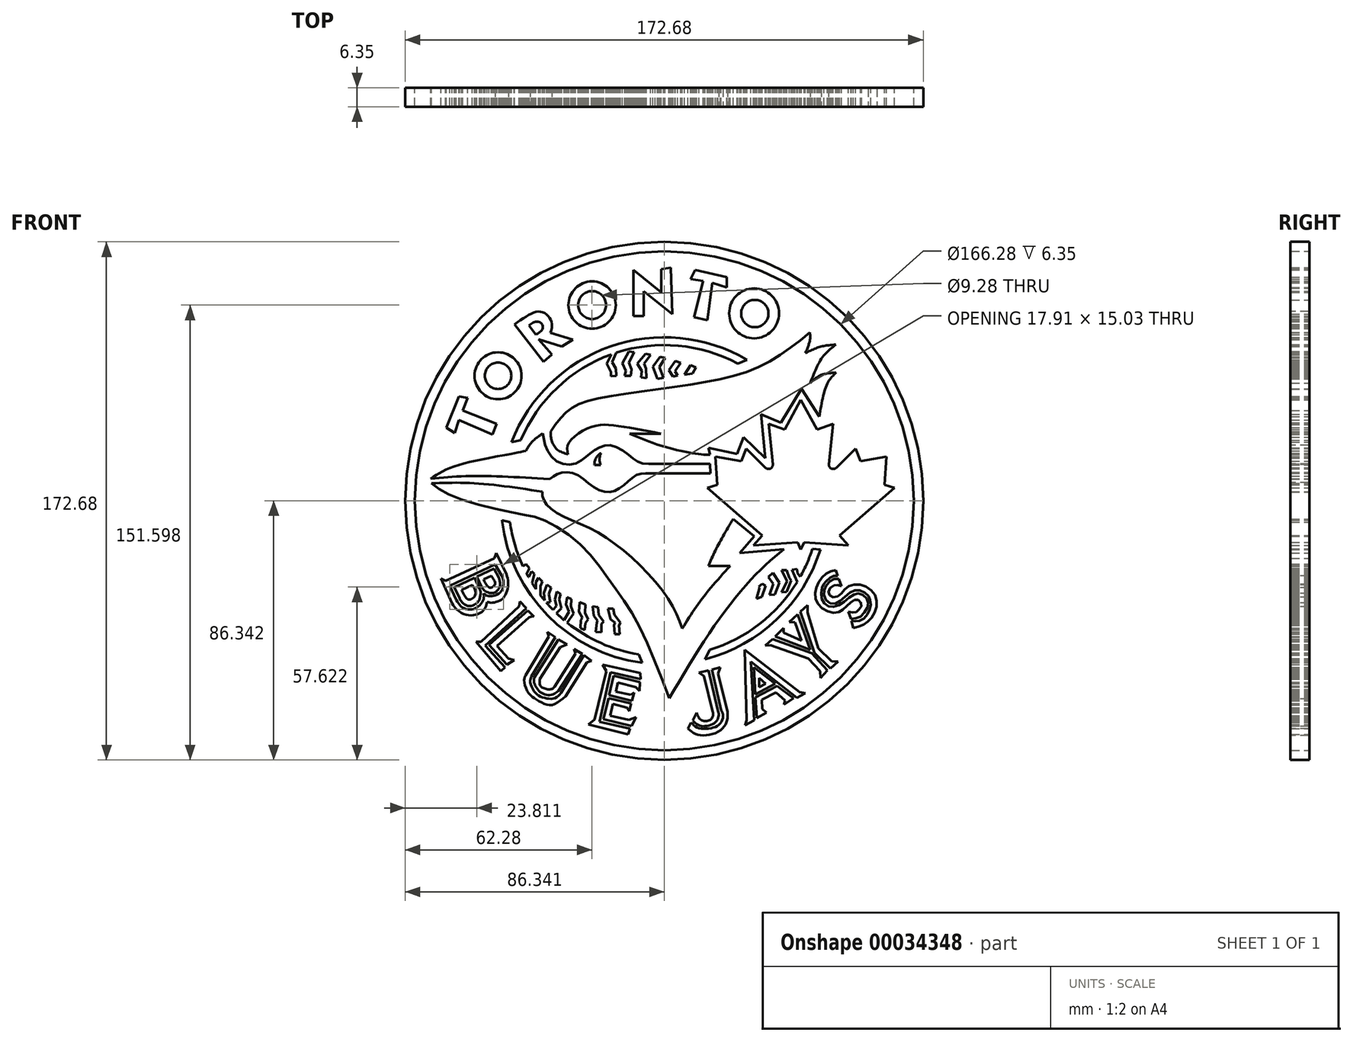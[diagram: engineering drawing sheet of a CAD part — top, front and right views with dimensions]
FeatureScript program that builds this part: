
annotation { "Feature Type Name" : "Feature", "Feature Type Description" : "" }
export const myFeature = defineFeature(function(context is Context, id is Id, definition is map)
    precondition{}
    {
        {
            var Q0;
            Q0=qCreatedBy(makeId("Front.planeOp"),FACE);
            var sketch = newSketch(context, id + "F0", { "sketchPlane" : qUnion([Q0])});
            skCircle(sketch, "E0", {"center": v(103.03, 95.92) * mm, "radius": 91.5 * mm});
            skCircle(sketch, "E1", {"center": v(103.03, 95.92) * mm, "radius": 88.78 * mm});
            skCircle(sketch, "E2", {"center": v(103.03, 95.92) * mm, "radius": 86.34 * mm});
            skCircle(sketch, "E3", {"center": v(103.03, 95.92) * mm, "radius": 83.14 * mm});
            skArc(sketch, "E4", {"start": v(48.91, 89.4) * mm, "mid": v(64.18, 57.7) * mm, "end": v(95.65, 41.92) * mm});
            skArc(sketch, "E5", {"start": v(51.6, 88.83) * mm, "mid": v(65.81, 59.73) * mm, "end": v(94.5, 44.71) * mm});
            skLineSegment(sketch, "E6", {"start": v(52.14, 115.45) * mm, "end": v(55.2, 116.12) * mm});
            skLineSegment(sketch, "E7", {"start": v(48.91, 89.4) * mm, "end": v(51.6, 88.83) * mm});
            skLineSegment(sketch, "E8", {"start": v(94.5, 44.71) * mm, "end": v(95.65, 41.92) * mm});
            skLineSegment(sketch, "E9", {"start": v(118.16, 46.26) * mm, "end": v(116.6, 43.13) * mm});
            skArc(sketch, "E10.trimOffspring", {"start": v(118.16, 46.26) * mm, "mid": v(139.41, 58.89) * mm, "end": v(152.42, 79.91) * mm});
            skArc(sketch, "E11.trimOffspring", {"start": v(116.6, 43.13) * mm, "mid": v(140.56, 56.4) * mm, "end": v(155.05, 79.63) * mm});
            skLineSegment(sketch, "E12", {"start": v(152.42, 79.91) * mm, "end": v(155.05, 79.63) * mm});
            skLineSegment(sketch, "E13", {"start": v(127.53, 141.7) * mm, "end": v(130.6, 142.95) * mm});
            skArc(sketch, "E14.trimOffspring", {"start": v(130.6, 142.95) * mm, "mid": v(85, 147.36) * mm, "end": v(52.14, 115.45) * mm});
            skArc(sketch, "E15.trimOffspring", {"start": v(127.53, 141.7) * mm, "mid": v(85.72, 144.87) * mm, "end": v(55.2, 116.12) * mm});
            skLineSegment(sketch, "E16", {"start": v(148.56, 129.54) * mm, "end": v(148.56, 79.7) * mm, "construction": true});
            skLineSegment(sketch, "E17", {"start": v(148.56, 129.54) * mm, "end": v(143.12, 119.66) * mm});
            skLineSegment(sketch, "E18", {"start": v(143.12, 119.66) * mm, "end": v(137.77, 121.56) * mm});
            skLineSegment(sketch, "E19", {"start": v(137.77, 121.56) * mm, "end": v(139.22, 108.15) * mm});
            skArc(sketch, "E20", {"start": v(139.22, 108.15) * mm, "mid": v(138.36, 106.66) * mm, "end": v(136.67, 107.03) * mm});
            skLineSegment(sketch, "E21", {"start": v(136.67, 107.03) * mm, "end": v(130.34, 113.34) * mm});
            skLineSegment(sketch, "E22", {"start": v(130.34, 113.34) * mm, "end": v(128.69, 109.14) * mm});
            skLineSegment(sketch, "E23", {"start": v(128.69, 109.14) * mm, "end": v(120, 110.7) * mm});
            skLineSegment(sketch, "E24", {"start": v(120, 110.7) * mm, "end": v(120.67, 101.3) * mm});
            skLineSegment(sketch, "E25", {"start": v(120.67, 101.3) * mm, "end": v(117.33, 100.22) * mm});
            skLineSegment(sketch, "E26", {"start": v(117.33, 100.22) * mm, "end": v(135.67, 84.42) * mm});
            skLineSegment(sketch, "E27", {"start": v(135.67, 84.42) * mm, "end": v(132.77, 81.06) * mm});
            skLineSegment(sketch, "E28", {"start": v(132.77, 81.06) * mm, "end": v(147.48, 82.1) * mm});
            skLineSegment(sketch, "E29", {"start": v(147.48, 82.1) * mm, "end": v(148.56, 79.7) * mm});
            skLineSegment(sketch, "E30.MirrorCS", {"start": v(176.45, 101.3) * mm, "end": v(179.78, 100.22) * mm});
            skLineSegment(sketch, "E31.MirrorCS", {"start": v(161.45, 84.42) * mm, "end": v(164.34, 81.06) * mm});
            skLineSegment(sketch, "E32.MirrorCS", {"start": v(166.78, 113.34) * mm, "end": v(168.43, 109.14) * mm});
            skArc(sketch, "E33.MirrorCS", {"start": v(157.9, 108.15) * mm, "mid": v(158.76, 106.66) * mm, "end": v(160.44, 107.03) * mm});
            skLineSegment(sketch, "E34.MirrorCS", {"start": v(149.64, 82.1) * mm, "end": v(148.56, 79.7) * mm});
            skLineSegment(sketch, "E35.MirrorCS", {"start": v(164.34, 81.06) * mm, "end": v(149.64, 82.1) * mm});
            skLineSegment(sketch, "E36.MirrorCS", {"start": v(159.34, 121.56) * mm, "end": v(157.9, 108.15) * mm});
            skLineSegment(sketch, "E37.MirrorCS", {"start": v(154, 119.66) * mm, "end": v(159.34, 121.56) * mm});
            skLineSegment(sketch, "E38.MirrorCS", {"start": v(160.44, 107.03) * mm, "end": v(166.78, 113.34) * mm});
            skLineSegment(sketch, "E39.MirrorCS", {"start": v(177.1, 110.7) * mm, "end": v(176.45, 101.3) * mm});
            skLineSegment(sketch, "E40.MirrorCS", {"start": v(168.43, 109.14) * mm, "end": v(177.1, 110.7) * mm});
            skLineSegment(sketch, "E41.MirrorCS", {"start": v(148.56, 129.54) * mm, "end": v(154, 119.66) * mm});
            skLineSegment(sketch, "E42.MirrorCS", {"start": v(179.78, 100.22) * mm, "end": v(161.45, 84.42) * mm});
            skFitSpline(sketch, "E43", {"points": [v(65.16, 119.04) * mm, v(70.66, 125.76) * mm, v(79.5, 129.73) * mm, v(109.43, 134.3) * mm, v(134.92, 140.72) * mm, v(151.56, 152.02) * mm], "startDerivative": vector(37.03, 53.23) * mm, "endDerivative": vector(73.6, 59.4) * mm});
            skFitSpline(sketch, "E44", {"points": [v(70.96, 111.41) * mm, v(71.11, 115.08) * mm, v(78.29, 120.42) * mm, v(86.53, 121.03) * mm, v(101.9, 118.34) * mm], "startDerivative": vector(-4.68, 21.83) * mm, "endDerivative": vector(49.53, -9.74) * mm});
            skFitSpline(sketch, "E45", {"points": [v(91.5, 118.29) * mm, v(103.51, 113.83) * mm, v(114.3, 111.55) * mm, v(118.26, 111.24) * mm], "startDerivative": vector(29.11, -12.06) * mm, "endDerivative": vector(15.42, -0.64) * mm});
            skFitSpline(sketch, "E46", {"points": [v(25.2, 103.34) * mm, v(32.9, 107.34) * mm, v(50.65, 111.34) * mm, v(56.95, 112.56) * mm], "startDerivative": vector(20.92, 13.84) * mm, "endDerivative": vector(19.98, 4) * mm});
            skFitSpline(sketch, "E47", {"points": [v(25.44, 101.77) * mm, v(33.14, 97.16) * mm, v(53.44, 91.83) * mm, v(62.71, 89.59) * mm, v(75.1, 81.35) * mm, v(85.16, 68.85) * mm, v(93.88, 55.68) * mm, v(104.66, 30.12) * mm], "startDerivative": vector(57.19, -43.62) * mm, "endDerivative": vector(55.75, -147.62) * mm});
            skFitSpline(sketch, "E48", {"points": [v(142.86, 79.86) * mm, v(133.46, 71.3) * mm, v(119.83, 54.38) * mm, v(104.66, 30.12) * mm], "startDerivative": vector(-34.83, -29.36) * mm, "endDerivative": vector(-37.83, -63.75) * mm});
            skFitSpline(sketch, "E49", {"points": [v(62.36, 98.98) * mm, v(62.87, 96.15) * mm, v(67, 92.01) * mm, v(78.22, 86.76) * mm, v(92.16, 77.06) * mm, v(104.58, 62.92) * mm, v(109.02, 53.43) * mm], "startDerivative": vector(1.07, -31.73) * mm, "endDerivative": vector(20.44, -54.43) * mm});
            skFitSpline(sketch, "E50", {"points": [v(109.02, 53.43) * mm, v(115.59, 63.23) * mm, v(124.98, 74.23) * mm], "startDerivative": vector(12.88, 20.58) * mm, "endDerivative": vector(18.93, 21.03) * mm});
            skFitSpline(sketch, "E51", {"points": [v(126, 89.89) * mm, v(120.94, 81.1) * mm, v(117.7, 74.23) * mm], "startDerivative": vector(-10.08, -16.82) * mm, "endDerivative": vector(-6.4, -14.44) * mm});
            skFitSpline(sketch, "E52", {"points": [v(62.56, 118.37) * mm, v(63.68, 113.62) * mm, v(67.72, 108.78) * mm, v(73.67, 108.47) * mm, v(77.51, 111.1) * mm, v(81.25, 113.62) * mm, v(85.29, 114.43) * mm, v(91.15, 111.2) * mm, v(94.78, 108.68) * mm, v(100.03, 108.27) * mm], "startDerivative": vector(6.02, -43.1) * mm, "endDerivative": vector(50.83, 1.53) * mm});
            skFitSpline(sketch, "E53", {"points": [v(64.79, 103.12) * mm, v(68.3, 105.12) * mm, v(73.58, 104.78) * mm, v(79.92, 100.18) * mm, v(85.37, 98.95) * mm, v(89.97, 101.53) * mm, v(94.06, 104.67) * mm, v(98.1, 105.06) * mm, v(100.85, 105.06) * mm], "startDerivative": vector(28.53, 20.8) * mm, "endDerivative": vector(27.63, 0.43) * mm});
            skFitSpline(sketch, "E54", {"points": [v(62.56, 118.37) * mm, v(61.23, 117.5) * mm, v(58.68, 115.27) * mm, v(56.95, 112.56) * mm], "startDerivative": vector(-4.68, -2.94) * mm, "endDerivative": vector(-4.02, -7.62) * mm});
            skFitSpline(sketch, "E55", {"points": [v(65.16, 119.04) * mm, v(65.44, 116.26) * mm, v(67.25, 113.1) * mm, v(70.96, 111.41) * mm], "startDerivative": vector(0.16, -9.06) * mm, "endDerivative": vector(11.34, -3.4) * mm});
            skFitSpline(sketch, "E56", {"points": [v(91.5, 118.29) * mm, v(101.9, 118.34) * mm], "startDerivative": vector(10.39, 0.05) * mm, "endDerivative": vector(10.39, 0.05) * mm});
            skLineSegment(sketch, "E57", {"start": v(118.26, 111.24) * mm, "end": v(117.8, 113.52) * mm});
            skLineSegment(sketch, "E58", {"start": v(117.8, 113.52) * mm, "end": v(127.26, 111.55) * mm});
            skLineSegment(sketch, "E59", {"start": v(127.26, 111.55) * mm, "end": v(129.43, 117.08) * mm});
            skLineSegment(sketch, "E60", {"start": v(129.43, 117.08) * mm, "end": v(136.65, 110.13) * mm});
            skLineSegment(sketch, "E61", {"start": v(136.65, 110.13) * mm, "end": v(135.36, 124.82) * mm});
            skLineSegment(sketch, "E62", {"start": v(135.36, 124.82) * mm, "end": v(141.96, 122.02) * mm});
            skLineSegment(sketch, "E63", {"start": v(141.96, 122.02) * mm, "end": v(148.7, 133.3) * mm});
            skLineSegment(sketch, "E64", {"start": v(148.7, 133.3) * mm, "end": v(154.7, 124.04) * mm});
            skFitSpline(sketch, "E65", {"points": [v(151.56, 152.02) * mm, v(151.56, 149.4) * mm, v(150.04, 145.15) * mm], "startDerivative": vector(0.58, -5.75) * mm, "endDerivative": vector(-3.44, -7.9) * mm});
            skFitSpline(sketch, "E66", {"points": [v(150.04, 145.15) * mm, v(155.23, 147.32) * mm, v(160.17, 147.96) * mm], "startDerivative": vector(10.04, 4.97) * mm, "endDerivative": vector(10.22, 0.62) * mm});
            skFitSpline(sketch, "E67", {"points": [v(160.17, 147.96) * mm, v(155.62, 143.57) * mm, v(151.67, 135.16) * mm], "startDerivative": vector(-10.7, -8.46) * mm, "endDerivative": vector(-6.44, -16.87) * mm});
            skFitSpline(sketch, "E68", {"points": [v(151.67, 135.16) * mm, v(155.13, 137.78) * mm, v(160.32, 138.67) * mm], "startDerivative": vector(6.64, 6.4) * mm, "endDerivative": vector(10.59, 0.7) * mm});
            skFitSpline(sketch, "E69", {"points": [v(160.32, 138.67) * mm, v(157.35, 134.97) * mm, v(154.7, 124.04) * mm], "startDerivative": vector(-8.15, -7.72) * mm, "endDerivative": vector(-3.43, -20.64) * mm});
            skLineSegment(sketch, "E70", {"start": v(100.03, 108.27) * mm, "end": v(118.29, 108.27) * mm});
            skLineSegment(sketch, "E71", {"start": v(118.29, 108.27) * mm, "end": v(118.43, 105.08) * mm});
            skLineSegment(sketch, "E72", {"start": v(118.43, 105.08) * mm, "end": v(100.85, 105.06) * mm});
            skFitSpline(sketch, "E73", {"points": [v(25.2, 103.34) * mm, v(40.41, 104.2) * mm, v(64.79, 103.12) * mm], "startDerivative": vector(32.45, 2.81) * mm, "endDerivative": vector(46.2, -3.04) * mm});
            skFitSpline(sketch, "E74", {"points": [v(25.44, 101.77) * mm, v(40.11, 101.77) * mm, v(62.36, 98.98) * mm], "startDerivative": vector(31.15, 1.13) * mm, "endDerivative": vector(42.3, -6.44) * mm});
            skLineSegment(sketch, "E75", {"start": v(126, 89.89) * mm, "end": v(132.96, 84.08) * mm});
            skLineSegment(sketch, "E76", {"start": v(132.96, 84.08) * mm, "end": v(128.14, 78.59) * mm});
            skLineSegment(sketch, "E77", {"start": v(128.14, 78.59) * mm, "end": v(142.86, 79.86) * mm});
            skLineSegment(sketch, "E78", {"start": v(124.98, 74.23) * mm, "end": v(117.7, 74.23) * mm});
            skCircle(sketch, "E79", {"center": v(133.2, 158.35) * mm, "radius": 4.55 * mm});
            skCircle(sketch, "E80", {"center": v(132.99, 158.42) * mm, "radius": 8.32 * mm});
            skLineSegment(sketch, "E81", {"start": v(117.34, 156.16) * mm, "end": v(112.99, 157.08) * mm});
            skLineSegment(sketch, "E82", {"start": v(112.99, 157.08) * mm, "end": v(115.93, 169.2) * mm});
            skLineSegment(sketch, "E83", {"start": v(115.93, 169.2) * mm, "end": v(111.8, 169.9) * mm});
            skLineSegment(sketch, "E84", {"start": v(111.8, 169.9) * mm, "end": v(113.28, 172.88) * mm});
            skLineSegment(sketch, "E85", {"start": v(113.28, 172.88) * mm, "end": v(123.86, 170.47) * mm});
            skLineSegment(sketch, "E86", {"start": v(123.86, 170.47) * mm, "end": v(123.86, 167) * mm});
            skLineSegment(sketch, "E87", {"start": v(123.86, 167) * mm, "end": v(118.98, 168.56) * mm});
            skLineSegment(sketch, "E88", {"start": v(118.98, 168.56) * mm, "end": v(117.34, 156.16) * mm});
            skLineSegment(sketch, "E89", {"start": v(105.18, 173.64) * mm, "end": v(105.75, 158.2) * mm});
            skLineSegment(sketch, "E90", {"start": v(105.75, 158.2) * mm, "end": v(96.18, 165.76) * mm});
            skLineSegment(sketch, "E91", {"start": v(96.18, 165.76) * mm, "end": v(96.18, 157.5) * mm});
            skLineSegment(sketch, "E92", {"start": v(96.18, 157.5) * mm, "end": v(92.75, 157.5) * mm});
            skLineSegment(sketch, "E93", {"start": v(92.75, 157.5) * mm, "end": v(92.75, 172.85) * mm});
            skLineSegment(sketch, "E94", {"start": v(92.75, 172.85) * mm, "end": v(101.96, 165.43) * mm});
            skLineSegment(sketch, "E95", {"start": v(101.96, 165.43) * mm, "end": v(101.96, 173.11) * mm});
            skLineSegment(sketch, "E96", {"start": v(101.96, 173.11) * mm, "end": v(105.18, 173.64) * mm});
            skCircle(sketch, "E97", {"center": v(78.97, 161.18) * mm, "radius": 4.64 * mm});
            skCircle(sketch, "E98", {"center": v(78.97, 161.18) * mm, "radius": 7.88 * mm});
            skCircle(sketch, "E99", {"center": v(47.64, 137.6) * mm, "radius": 7.83 * mm});
            skCircle(sketch, "E100", {"center": v(47.64, 137.6) * mm, "radius": 4.42 * mm});
            skLineSegment(sketch, "E101", {"start": v(47.13, 121.57) * mm, "end": v(35.88, 126.05) * mm});
            skLineSegment(sketch, "E102", {"start": v(35.88, 126.05) * mm, "end": v(37.5, 130.2) * mm});
            skLineSegment(sketch, "E103", {"start": v(37.5, 130.2) * mm, "end": v(34.61, 130.7) * mm});
            skLineSegment(sketch, "E104", {"start": v(34.61, 130.7) * mm, "end": v(30.33, 120.34) * mm});
            skLineSegment(sketch, "E105", {"start": v(30.33, 120.34) * mm, "end": v(33.17, 118.56) * mm});
            skLineSegment(sketch, "E106", {"start": v(33.17, 118.56) * mm, "end": v(34.54, 122.86) * mm});
            skLineSegment(sketch, "E107", {"start": v(34.54, 122.86) * mm, "end": v(45.75, 118.08) * mm});
            skLineSegment(sketch, "E108", {"start": v(45.75, 118.08) * mm, "end": v(47.13, 121.57) * mm});
            skLineSegment(sketch, "E109", {"start": v(53.13, 154.75) * mm, "end": v(62.81, 142.26) * mm});
            skLineSegment(sketch, "E110", {"start": v(62.81, 142.26) * mm, "end": v(65.59, 144.65) * mm});
            skLineSegment(sketch, "E111", {"start": v(65.59, 144.65) * mm, "end": v(61.17, 149.8) * mm});
            skLineSegment(sketch, "E112", {"start": v(61.17, 149.8) * mm, "end": v(68.92, 147.33) * mm});
            skLineSegment(sketch, "E113", {"start": v(68.92, 147.33) * mm, "end": v(72.5, 149.7) * mm});
            skLineSegment(sketch, "E114", {"start": v(72.5, 149.7) * mm, "end": v(65.1, 152) * mm});
            skFitSpline(sketch, "E115", {"points": [v(53.13, 154.75) * mm, v(59.13, 158.49) * mm, v(62.38, 158.83) * mm, v(65.01, 156.6) * mm, v(65.61, 153.93) * mm, v(65.1, 152) * mm], "startDerivative": vector(22.47, 15.8) * mm, "endDerivative": vector(-4.46, -12.2) * mm});
            skFitSpline(sketch, "E116", {"points": [v(57.9, 154.3) * mm, v(59.68, 155.53) * mm, v(61.75, 155.36) * mm, v(62.57, 153.73) * mm, v(61.64, 152.27) * mm, v(60.24, 151.35) * mm], "startDerivative": vector(7.67, 6.93) * mm, "endDerivative": vector(-7.62, -4.34) * mm});
            skLineSegment(sketch, "E117", {"start": v(57.9, 154.3) * mm, "end": v(60.24, 151.35) * mm});
            skLineSegment(sketch, "E118", {"start": v(40.25, 48.97) * mm, "end": v(48.5, 39.18) * mm});
            skLineSegment(sketch, "E119", {"start": v(48.5, 39.18) * mm, "end": v(49.91, 40.37) * mm});
            skLineSegment(sketch, "E120", {"start": v(49.91, 40.37) * mm, "end": v(43.3, 47.7) * mm});
            skLineSegment(sketch, "E121", {"start": v(43.3, 47.7) * mm, "end": v(57.13, 60.17) * mm});
            skLineSegment(sketch, "E122", {"start": v(57.13, 60.17) * mm, "end": v(54.87, 62.4) * mm});
            skLineSegment(sketch, "E123", {"start": v(59.58, 57.34) * mm, "end": v(57.5, 59.39) * mm});
            skLineSegment(sketch, "E124", {"start": v(57.5, 59.39) * mm, "end": v(44.68, 47.88) * mm});
            skLineSegment(sketch, "E125", {"start": v(44.68, 47.88) * mm, "end": v(50.6, 41.28) * mm});
            skLineSegment(sketch, "E126", {"start": v(50.6, 41.28) * mm, "end": v(52.98, 42.9) * mm});
            skLineSegment(sketch, "E127", {"start": v(52.98, 42.9) * mm, "end": v(51.13, 43.4) * mm});
            skLineSegment(sketch, "E128", {"start": v(51.13, 43.4) * mm, "end": v(47.24, 47.57) * mm});
            skLineSegment(sketch, "E129", {"start": v(47.24, 47.57) * mm, "end": v(57.89, 57.12) * mm});
            skLineSegment(sketch, "E130", {"start": v(57.89, 57.12) * mm, "end": v(59.14, 57.4) * mm});
            skLineSegment(sketch, "E131", {"start": v(59.14, 57.4) * mm, "end": v(59.58, 57.34) * mm});
            skLineSegment(sketch, "E132", {"start": v(95, 38.48) * mm, "end": v(82.45, 41.28) * mm});
            skLineSegment(sketch, "E133", {"start": v(82.45, 41.28) * mm, "end": v(83.69, 39.12) * mm});
            skLineSegment(sketch, "E134", {"start": v(83.69, 39.12) * mm, "end": v(79.75, 23.01) * mm});
            skLineSegment(sketch, "E135", {"start": v(79.75, 23.01) * mm, "end": v(77.74, 21.38) * mm});
            skLineSegment(sketch, "E136", {"start": v(77.74, 21.38) * mm, "end": v(91.03, 18.03) * mm});
            skLineSegment(sketch, "E137", {"start": v(91.03, 18.03) * mm, "end": v(91.65, 20.03) * mm});
            skLineSegment(sketch, "E138", {"start": v(91.65, 20.03) * mm, "end": v(81.45, 22.33) * mm});
            skLineSegment(sketch, "E139", {"start": v(81.45, 22.33) * mm, "end": v(85.14, 38.75) * mm});
            skLineSegment(sketch, "E140", {"start": v(85.14, 38.75) * mm, "end": v(95.15, 36.45) * mm});
            skLineSegment(sketch, "E141", {"start": v(95.15, 36.45) * mm, "end": v(95, 38.48) * mm});
            skLineSegment(sketch, "E142", {"start": v(94.95, 35.48) * mm, "end": v(86.1, 37.6) * mm});
            skLineSegment(sketch, "E143", {"start": v(86.1, 37.6) * mm, "end": v(84.57, 31.17) * mm});
            skLineSegment(sketch, "E144", {"start": v(84.57, 31.17) * mm, "end": v(92.28, 29.28) * mm});
            skLineSegment(sketch, "E145", {"start": v(92.28, 29.28) * mm, "end": v(92.97, 32.08) * mm});
            skLineSegment(sketch, "E146", {"start": v(92.97, 32.08) * mm, "end": v(91.8, 31.26) * mm});
            skLineSegment(sketch, "E147", {"start": v(91.8, 31.26) * mm, "end": v(86.87, 32.25) * mm});
            skLineSegment(sketch, "E148", {"start": v(86.87, 32.25) * mm, "end": v(87.55, 35.33) * mm});
            skLineSegment(sketch, "E149", {"start": v(87.55, 35.33) * mm, "end": v(93.45, 33.78) * mm});
            skLineSegment(sketch, "E150", {"start": v(93.45, 33.78) * mm, "end": v(94.77, 32.5) * mm});
            skLineSegment(sketch, "E151", {"start": v(94.77, 32.5) * mm, "end": v(94.95, 35.48) * mm});
            skLineSegment(sketch, "E152", {"start": v(84.5, 30.19) * mm, "end": v(92, 28.35) * mm});
            skLineSegment(sketch, "E153", {"start": v(92, 28.35) * mm, "end": v(91.41, 25.89) * mm});
            skLineSegment(sketch, "E154", {"start": v(91.41, 25.89) * mm, "end": v(90.56, 27) * mm});
            skLineSegment(sketch, "E155", {"start": v(90.56, 27) * mm, "end": v(85.9, 28.29) * mm});
            skLineSegment(sketch, "E156", {"start": v(85.9, 28.29) * mm, "end": v(85.02, 24.3) * mm});
            skLineSegment(sketch, "E157", {"start": v(85.02, 24.3) * mm, "end": v(91.25, 22.9) * mm});
            skLineSegment(sketch, "E158", {"start": v(91.25, 22.9) * mm, "end": v(93.6, 23.76) * mm});
            skLineSegment(sketch, "E159", {"start": v(93.6, 23.76) * mm, "end": v(92.11, 20.9) * mm});
            skLineSegment(sketch, "E160", {"start": v(92.11, 20.9) * mm, "end": v(82.77, 23.11) * mm});
            skLineSegment(sketch, "E161", {"start": v(82.77, 23.11) * mm, "end": v(84.5, 30.19) * mm});
            skLineSegment(sketch, "E162", {"start": v(28.6, 70) * mm, "end": v(30.08, 69.23) * mm});
            skLineSegment(sketch, "E163", {"start": v(30.08, 69.23) * mm, "end": v(46.46, 76.7) * mm});
            skLineSegment(sketch, "E164", {"start": v(46.46, 76.7) * mm, "end": v(47.04, 78.52) * mm});
            skLineSegment(sketch, "E165", {"start": v(47.04, 78.52) * mm, "end": v(50.44, 71.43) * mm});
            skLineSegment(sketch, "E166", {"start": v(28.6, 70) * mm, "end": v(32.27, 61.75) * mm});
            skLineSegment(sketch, "E167", {"start": v(40.25, 48.97) * mm, "end": v(42, 48.97) * mm});
            skLineSegment(sketch, "E168", {"start": v(42, 48.97) * mm, "end": v(54.6, 60.71) * mm});
            skLineSegment(sketch, "E169", {"start": v(54.6, 60.71) * mm, "end": v(54.87, 62.4) * mm});
            skLineSegment(sketch, "E170", {"start": v(64.02, 52.3) * mm, "end": v(66.72, 50.48) * mm});
            skLineSegment(sketch, "E171", {"start": v(66.72, 50.48) * mm, "end": v(58.73, 37.32) * mm});
            skLineSegment(sketch, "E172", {"start": v(70.66, 48) * mm, "end": v(67.73, 49.76) * mm});
            skLineSegment(sketch, "E173", {"start": v(67.73, 49.76) * mm, "end": v(59.6, 36.83) * mm});
            skLineSegment(sketch, "E174", {"start": v(72.95, 46.55) * mm, "end": v(73.47, 45.05) * mm});
            skLineSegment(sketch, "E175", {"start": v(73.47, 45.05) * mm, "end": v(66.45, 34) * mm});
            skLineSegment(sketch, "E176", {"start": v(72.95, 46.55) * mm, "end": v(75.7, 44.84) * mm});
            skLineSegment(sketch, "E177", {"start": v(75.7, 44.84) * mm, "end": v(67.7, 32.5) * mm});
            skLineSegment(sketch, "E178", {"start": v(61.56, 36.52) * mm, "end": v(68.36, 47.17) * mm});
            skLineSegment(sketch, "E179", {"start": v(68.36, 47.17) * mm, "end": v(70.66, 48) * mm});
            skLineSegment(sketch, "E180", {"start": v(70.15, 30.8) * mm, "end": v(77.21, 42.1) * mm});
            skLineSegment(sketch, "E181", {"start": v(77.21, 42.1) * mm, "end": v(78.77, 42.64) * mm});
            skLineSegment(sketch, "E182", {"start": v(78.77, 42.64) * mm, "end": v(76.2, 44.43) * mm});
            skLineSegment(sketch, "E183", {"start": v(76.2, 44.43) * mm, "end": v(68.68, 31.88) * mm});
            skFitSpline(sketch, "E184", {"points": [v(58.73, 37.32) * mm, v(58.36, 35.74) * mm, v(59.93, 32.06) * mm, v(62.76, 30.36) * mm, v(66.28, 30.06) * mm, v(68.68, 31.88) * mm], "startDerivative": vector(-4.2, -9.31) * mm, "endDerivative": vector(10.8, 11.52) * mm});
            skFitSpline(sketch, "E185", {"points": [v(59.6, 36.83) * mm, v(59.6, 35.55) * mm, v(60.61, 33.4) * mm, v(62.63, 31.6) * mm, v(65.56, 31.31) * mm, v(67.7, 32.5) * mm], "startDerivative": vector(-0.96, -8.08) * mm, "endDerivative": vector(9.5, 7.15) * mm});
            skFitSpline(sketch, "E186", {"points": [v(66.45, 34) * mm, v(65.38, 33.15) * mm, v(62.01, 34) * mm, v(61.56, 36.52) * mm], "startDerivative": vector(-2.97, -4.2) * mm, "endDerivative": vector(0.77, 8.19) * mm});
            skLineSegment(sketch, "E187", {"start": v(64.02, 52.3) * mm, "end": v(64.62, 50.68) * mm});
            skLineSegment(sketch, "E188", {"start": v(64.62, 50.68) * mm, "end": v(56.82, 37.76) * mm});
            skFitSpline(sketch, "E189", {"points": [v(56.82, 37.76) * mm, v(56.3, 36.04) * mm, v(57.8, 31.85) * mm, v(60.95, 29.38) * mm, v(65.2, 27.82) * mm, v(70.15, 30.8) * mm], "startDerivative": vector(-5.74, -10.9) * mm, "endDerivative": vector(20.48, 17.81) * mm});
            skLineSegment(sketch, "E190", {"start": v(31.55, 67.65) * mm, "end": v(46.66, 74.72) * mm});
            skLineSegment(sketch, "E191", {"start": v(46.66, 74.72) * mm, "end": v(48.82, 70.99) * mm});
            skLineSegment(sketch, "E192", {"start": v(31.55, 67.65) * mm, "end": v(33.76, 62.92) * mm});
            skLineSegment(sketch, "E193", {"start": v(34.8, 63.38) * mm, "end": v(33.01, 67.08) * mm});
            skLineSegment(sketch, "E194", {"start": v(33.01, 67.08) * mm, "end": v(39.75, 70.32) * mm});
            skLineSegment(sketch, "E195", {"start": v(39.75, 70.32) * mm, "end": v(41.43, 66.63) * mm});
            skLineSegment(sketch, "E196", {"start": v(42.2, 67.1) * mm, "end": v(40.53, 70.66) * mm});
            skLineSegment(sketch, "E197", {"start": v(40.53, 70.66) * mm, "end": v(46.28, 73.37) * mm});
            skLineSegment(sketch, "E198", {"start": v(46.28, 73.37) * mm, "end": v(47.9, 70.3) * mm});
            skLineSegment(sketch, "E199", {"start": v(42.8, 69.72) * mm, "end": v(45.33, 70.95) * mm});
            skLineSegment(sketch, "E200", {"start": v(35.46, 66.18) * mm, "end": v(39.02, 67.91) * mm});
            skFitSpline(sketch, "E201", {"points": [v(39.02, 67.91) * mm, v(39.91, 66.3) * mm, v(40.15, 64.94) * mm, v(39.22, 63.42) * mm, v(37.63, 63.07) * mm, v(36.58, 64.07) * mm, v(35.46, 66.18) * mm], "startDerivative": vector(5.81, -9.56) * mm, "endDerivative": vector(-5.65, 11.5) * mm});
            skFitSpline(sketch, "E202", {"points": [v(34.8, 63.38) * mm, v(35.86, 61.87) * mm, v(38.1, 60.83) * mm, v(40.03, 61.44) * mm, v(41.32, 62.85) * mm, v(41.74, 65.83) * mm, v(41.43, 66.63) * mm], "startDerivative": vector(5.29, -9.62) * mm, "endDerivative": vector(-3.4, 5.59) * mm});
            skFitSpline(sketch, "E203", {"points": [v(42.2, 67.1) * mm, v(43.47, 65.74) * mm, v(45.9, 65.16) * mm, v(47, 65.7) * mm, v(48.25, 67.48) * mm, v(47.9, 70.3) * mm], "startDerivative": vector(5.31, -7.93) * mm, "endDerivative": vector(-3.66, 12.63) * mm});
            skFitSpline(sketch, "E204", {"points": [v(42.8, 69.72) * mm, v(43.67, 68.04) * mm, v(45.08, 67) * mm, v(46.56, 67.92) * mm, v(46.52, 69.02) * mm, v(45.33, 70.95) * mm], "startDerivative": vector(3.6, -8.13) * mm, "endDerivative": vector(-6.18, 8.91) * mm});
            skFitSpline(sketch, "E205", {"points": [v(50.44, 71.43) * mm, v(51.02, 67.81) * mm, v(49.81, 64.1) * mm, v(48.2, 62.7) * mm, v(45.62, 61.95) * mm, v(44.02, 62.2) * mm], "startDerivative": vector(4.3, -15.1) * mm, "endDerivative": vector(-9.55, 2.78) * mm});
            skFitSpline(sketch, "E206", {"points": [v(48.82, 70.99) * mm, v(49.43, 69.04) * mm, v(48.82, 66.01) * mm, v(46.24, 64.29) * mm, v(43.72, 64.4) * mm, v(42.82, 65.11) * mm], "startDerivative": vector(4.13, -9.46) * mm, "endDerivative": vector(-5.22, 5.63) * mm});
            skFitSpline(sketch, "E207", {"points": [v(42.82, 65.11) * mm, v(42.82, 63.3) * mm, v(41.41, 60.98) * mm, v(38.83, 59.73) * mm, v(35.78, 60.34) * mm, v(33.76, 62.92) * mm], "startDerivative": vector(1.41, -10.76) * mm, "endDerivative": vector(-7.82, 13.64) * mm});
            skFitSpline(sketch, "E208", {"points": [v(32.27, 61.75) * mm, v(34.1, 59.48) * mm, v(37.88, 57.8) * mm, v(40.9, 58.18) * mm, v(42.4, 59.05) * mm, v(43.62, 60.89) * mm, v(44.02, 62.2) * mm], "startDerivative": vector(8.33, -13.1) * mm, "endDerivative": vector(2.2, 10.01) * mm});
            skLineSegment(sketch, "E209", {"start": v(150.78, 61.08) * mm, "end": v(150.78, 58.72) * mm});
            skLineSegment(sketch, "E210", {"start": v(150.78, 58.72) * mm, "end": v(154.3, 46.82) * mm});
            skLineSegment(sketch, "E211", {"start": v(154.3, 46.82) * mm, "end": v(158.8, 42.5) * mm});
            skLineSegment(sketch, "E212", {"start": v(158.8, 42.5) * mm, "end": v(160.89, 42.38) * mm});
            skLineSegment(sketch, "E213", {"start": v(160.89, 42.38) * mm, "end": v(158.4, 40) * mm});
            skLineSegment(sketch, "E214", {"start": v(158.4, 40) * mm, "end": v(153.1, 45.26) * mm});
            skLineSegment(sketch, "E215", {"start": v(153.1, 45.26) * mm, "end": v(148.36, 59) * mm});
            skLineSegment(sketch, "E216", {"start": v(148.36, 59) * mm, "end": v(150.78, 61.08) * mm});
            skLineSegment(sketch, "E217", {"start": v(136.67, 47.68) * mm, "end": v(139.14, 49.8) * mm});
            skLineSegment(sketch, "E218", {"start": v(139.14, 49.8) * mm, "end": v(152.2, 45.1) * mm});
            skLineSegment(sketch, "E219", {"start": v(152.2, 45.1) * mm, "end": v(157.45, 39.39) * mm});
            skLineSegment(sketch, "E220", {"start": v(157.45, 39.39) * mm, "end": v(155.13, 36.86) * mm});
            skLineSegment(sketch, "E221", {"start": v(155.13, 36.86) * mm, "end": v(155.03, 39.19) * mm});
            skLineSegment(sketch, "E222", {"start": v(155.03, 39.19) * mm, "end": v(151.08, 43.33) * mm});
            skLineSegment(sketch, "E223", {"start": v(151.08, 43.33) * mm, "end": v(138.5, 47.78) * mm});
            skLineSegment(sketch, "E224", {"start": v(138.5, 47.78) * mm, "end": v(136.67, 47.68) * mm});
            skLineSegment(sketch, "E225", {"start": v(139.94, 50.68) * mm, "end": v(142.85, 53.55) * mm});
            skLineSegment(sketch, "E226", {"start": v(142.85, 53.55) * mm, "end": v(142.8, 52) * mm});
            skLineSegment(sketch, "E227", {"start": v(142.8, 52) * mm, "end": v(148.74, 49.31) * mm});
            skLineSegment(sketch, "E228", {"start": v(148.74, 49.31) * mm, "end": v(146.6, 55.43) * mm});
            skLineSegment(sketch, "E229", {"start": v(146.6, 55.43) * mm, "end": v(144.75, 55.48) * mm});
            skLineSegment(sketch, "E230", {"start": v(144.75, 55.48) * mm, "end": v(147.48, 58.07) * mm});
            skLineSegment(sketch, "E231", {"start": v(147.48, 58.07) * mm, "end": v(151.66, 46.3) * mm});
            skLineSegment(sketch, "E232", {"start": v(151.66, 46.3) * mm, "end": v(139.94, 50.68) * mm});
            skLineSegment(sketch, "E233", {"start": v(129.94, 21.18) * mm, "end": v(130.53, 22.78) * mm});
            skLineSegment(sketch, "E234", {"start": v(130.53, 22.78) * mm, "end": v(129.78, 46.31) * mm});
            skLineSegment(sketch, "E235", {"start": v(129.78, 46.31) * mm, "end": v(148.07, 32.15) * mm});
            skLineSegment(sketch, "E236", {"start": v(148.07, 32.15) * mm, "end": v(150.09, 31.84) * mm});
            skLineSegment(sketch, "E237", {"start": v(150.09, 31.84) * mm, "end": v(147.17, 30.3) * mm});
            skLineSegment(sketch, "E238", {"start": v(147.17, 30.3) * mm, "end": v(131.9, 42.28) * mm});
            skLineSegment(sketch, "E239", {"start": v(131.9, 42.28) * mm, "end": v(132.96, 22.77) * mm});
            skLineSegment(sketch, "E240", {"start": v(132.96, 22.77) * mm, "end": v(129.94, 21.18) * mm});
            skLineSegment(sketch, "E241", {"start": v(132.86, 40.46) * mm, "end": v(133.35, 31.4) * mm});
            skLineSegment(sketch, "E242", {"start": v(133.35, 31.4) * mm, "end": v(139.96, 34.95) * mm});
            skLineSegment(sketch, "E243", {"start": v(139.96, 34.95) * mm, "end": v(132.86, 40.46) * mm});
            skLineSegment(sketch, "E244", {"start": v(134.72, 36.81) * mm, "end": v(134.72, 33.88) * mm});
            skLineSegment(sketch, "E245", {"start": v(134.72, 33.88) * mm, "end": v(136.76, 34.99) * mm});
            skLineSegment(sketch, "E246", {"start": v(136.76, 34.99) * mm, "end": v(134.72, 36.81) * mm});
            skLineSegment(sketch, "E247", {"start": v(133.45, 30.37) * mm, "end": v(140.69, 34.24) * mm});
            skLineSegment(sketch, "E248", {"start": v(140.69, 34.24) * mm, "end": v(146.14, 30.1) * mm});
            skLineSegment(sketch, "E249", {"start": v(146.14, 30.1) * mm, "end": v(142.96, 28.02) * mm});
            skLineSegment(sketch, "E250", {"start": v(142.96, 28.02) * mm, "end": v(143.32, 29.37) * mm});
            skLineSegment(sketch, "E251", {"start": v(143.32, 29.37) * mm, "end": v(140.3, 32.08) * mm});
            skLineSegment(sketch, "E252", {"start": v(140.3, 32.08) * mm, "end": v(135.57, 29.62) * mm});
            skLineSegment(sketch, "E253", {"start": v(135.57, 29.62) * mm, "end": v(135.71, 26.6) * mm});
            skLineSegment(sketch, "E254", {"start": v(135.71, 26.6) * mm, "end": v(137.12, 25.26) * mm});
            skLineSegment(sketch, "E255", {"start": v(137.12, 25.26) * mm, "end": v(133.89, 23.51) * mm});
            skLineSegment(sketch, "E256", {"start": v(133.89, 23.51) * mm, "end": v(133.45, 30.37) * mm});
            skLineSegment(sketch, "E257", {"start": v(114.54, 38.65) * mm, "end": v(117.8, 39.43) * mm});
            skLineSegment(sketch, "E258", {"start": v(117.8, 39.43) * mm, "end": v(120.88, 26.3) * mm});
            skLineSegment(sketch, "E259", {"start": v(114.54, 38.65) * mm, "end": v(116.29, 37.5) * mm});
            skLineSegment(sketch, "E260", {"start": v(116.29, 37.5) * mm, "end": v(119.22, 25.56) * mm});
            skLineSegment(sketch, "E261", {"start": v(124.05, 26.2) * mm, "end": v(120.97, 38.33) * mm});
            skLineSegment(sketch, "E262", {"start": v(120.97, 38.33) * mm, "end": v(121.75, 40.49) * mm});
            skLineSegment(sketch, "E263", {"start": v(121.75, 40.49) * mm, "end": v(118.86, 39.66) * mm});
            skLineSegment(sketch, "E264", {"start": v(118.86, 39.66) * mm, "end": v(121.98, 26.2) * mm});
            skFitSpline(sketch, "E265", {"points": [v(124.05, 26.2) * mm, v(124.05, 23.07) * mm, v(121.42, 19.2) * mm, v(114.6, 17.88) * mm, v(110.93, 19.99) * mm], "startDerivative": vector(1.72, -14.8) * mm, "endDerivative": vector(-13.1, 11.2) * mm});
            skFitSpline(sketch, "E266", {"points": [v(111.98, 22.06) * mm, v(114.16, 20.3) * mm, v(118.53, 20.14) * mm, v(121.61, 21.59) * mm, v(122.63, 24.32) * mm, v(121.98, 26.2) * mm], "startDerivative": vector(9.62, -10.84) * mm, "endDerivative": vector(-5.75, 10.74) * mm});
            skFitSpline(sketch, "E267", {"points": [v(120.88, 26.3) * mm, v(121.16, 24.58) * mm, v(120.45, 22.51) * mm, v(117.93, 21.06) * mm, v(114.75, 21.01) * mm, v(112.55, 22.74) * mm], "startDerivative": vector(2.69, -9.99) * mm, "endDerivative": vector(-9.45, 10.05) * mm});
            skFitSpline(sketch, "E268", {"points": [v(119.22, 25.56) * mm, v(119.22, 24.15) * mm, v(118.11, 22.79) * mm, v(115.28, 22.86) * mm, v(113.84, 25.3) * mm], "startDerivative": vector(0.87, -6.97) * mm, "endDerivative": vector(-3.42, 10.28) * mm});
            skLineSegment(sketch, "E269", {"start": v(113.84, 25.3) * mm, "end": v(112.55, 22.74) * mm});
            skLineSegment(sketch, "E270", {"start": v(111.98, 22.06) * mm, "end": v(110.93, 19.99) * mm});
            skFitSpline(sketch, "E271", {"points": [v(160.12, 72.83) * mm, v(157.02, 71.66) * mm, v(154.14, 68.2) * mm, v(153.35, 64.15) * mm, v(155.33, 60.34) * mm, v(159.98, 58.62) * mm, v(162.8, 59.88) * mm, v(165.56, 62.34) * mm, v(167.51, 62.94) * mm, v(168.78, 61.36) * mm, v(167.99, 59.81) * mm, v(166.7, 58.74) * mm, v(164.37, 58.98) * mm], "startDerivative": vector(-36.46, -8.8) * mm, "endDerivative": vector(-35.06, 8.77) * mm});
            skFitSpline(sketch, "E272", {"points": [v(160.81, 70.92) * mm, v(158.9, 70.73) * mm, v(156.67, 68.7) * mm, v(155.67, 67.25) * mm, v(155.5, 63.44) * mm, v(157.62, 60.86) * mm, v(161.05, 61.05) * mm, v(165.34, 64.2) * mm, v(168.1, 65) * mm, v(170.59, 63.15) * mm, v(170.76, 60.48) * mm, v(168.23, 57.26) * mm, v(165.27, 56.6) * mm], "startDerivative": vector(-29.03, 2.77) * mm, "endDerivative": vector(-36.87, -1.87) * mm});
            skLineSegment(sketch, "E273", {"start": v(164.37, 58.98) * mm, "end": v(165.27, 56.6) * mm});
            skLineSegment(sketch, "E274", {"start": v(160.12, 72.83) * mm, "end": v(160.81, 70.92) * mm});
            skFitSpline(sketch, "E275", {"points": [v(161.23, 69.9) * mm, v(159.18, 69.73) * mm, v(156.98, 67.63) * mm, v(156.24, 65.4) * mm, v(157.03, 62.74) * mm, v(159.52, 61.63) * mm, v(162.12, 62.94) * mm, v(165.38, 65.68) * mm, v(167.85, 66.12) * mm, v(170.52, 64.86) * mm, v(171.53, 63.2) * mm, v(171.83, 61.08) * mm, v(170.9, 58.26) * mm, v(168.91, 56.31) * mm, v(166.72, 55.74) * mm, v(165.36, 55.87) * mm], "startDerivative": vector(-34.34, 3.2) * mm, "endDerivative": vector(-26.06, 4.32) * mm});
            skFitSpline(sketch, "E276", {"points": [v(162.07, 67.52) * mm, v(159.95, 67.84) * mm, v(157.78, 65.95) * mm, v(158.66, 64.02) * mm, v(161.33, 64.39) * mm, v(164.14, 67.3) * mm, v(169.12, 67.75) * mm, v(173.41, 64.16) * mm, v(173.18, 58.76) * mm, v(170.14, 55.07) * mm, v(166.08, 53.46) * mm], "startDerivative": vector(-26.81, 10.1) * mm, "endDerivative": vector(-39.52, -11.38) * mm});
            skLineSegment(sketch, "E277", {"start": v(165.36, 55.87) * mm, "end": v(166.08, 53.46) * mm});
            skLineSegment(sketch, "E278", {"start": v(161.23, 69.9) * mm, "end": v(162.07, 67.52) * mm});
            skLineSegment(sketch, "E279", {"start": v(111.8, 141.1) * mm, "end": v(113.64, 140.39) * mm});
            skLineSegment(sketch, "E280", {"start": v(113.64, 140.39) * mm, "end": v(112.39, 138.4) * mm});
            skLineSegment(sketch, "E281", {"start": v(112.39, 138.4) * mm, "end": v(109.78, 138.02) * mm});
            skLineSegment(sketch, "E282", {"start": v(109.78, 138.02) * mm, "end": v(111.8, 141.1) * mm});
            skLineSegment(sketch, "E283", {"start": v(106.78, 142.6) * mm, "end": v(108.49, 141.94) * mm});
            skLineSegment(sketch, "E284", {"start": v(108.49, 141.94) * mm, "end": v(106.62, 139.07) * mm});
            skLineSegment(sketch, "E285", {"start": v(106.62, 139.07) * mm, "end": v(107.47, 137.73) * mm});
            skLineSegment(sketch, "E286", {"start": v(107.47, 137.73) * mm, "end": v(105.99, 137.34) * mm});
            skLineSegment(sketch, "E287", {"start": v(105.99, 137.34) * mm, "end": v(104.6, 139.53) * mm});
            skLineSegment(sketch, "E288", {"start": v(104.6, 139.53) * mm, "end": v(106.78, 142.6) * mm});
            skLineSegment(sketch, "E289", {"start": v(101.58, 143.99) * mm, "end": v(103.32, 143.5) * mm});
            skLineSegment(sketch, "E290", {"start": v(103.32, 143.5) * mm, "end": v(101.39, 140.55) * mm});
            skLineSegment(sketch, "E291", {"start": v(101.39, 140.55) * mm, "end": v(102.82, 136.95) * mm});
            skLineSegment(sketch, "E292", {"start": v(102.82, 136.95) * mm, "end": v(100.8, 136.6) * mm});
            skLineSegment(sketch, "E293", {"start": v(100.8, 136.6) * mm, "end": v(99.28, 140.63) * mm});
            skLineSegment(sketch, "E294", {"start": v(99.28, 140.63) * mm, "end": v(101.58, 143.99) * mm});
            skLineSegment(sketch, "E295", {"start": v(96.82, 145) * mm, "end": v(98.52, 144.51) * mm});
            skLineSegment(sketch, "E296", {"start": v(98.52, 144.51) * mm, "end": v(96.31, 141.69) * mm});
            skLineSegment(sketch, "E297", {"start": v(96.31, 141.69) * mm, "end": v(96.96, 139.98) * mm});
            skLineSegment(sketch, "E298", {"start": v(96.96, 139.98) * mm, "end": v(97.09, 136.85) * mm});
            skLineSegment(sketch, "E299", {"start": v(97.09, 136.85) * mm, "end": v(95.35, 137.03) * mm});
            skLineSegment(sketch, "E300", {"start": v(95.35, 137.03) * mm, "end": v(95.5, 139.22) * mm});
            skLineSegment(sketch, "E301", {"start": v(95.5, 139.22) * mm, "end": v(94.08, 141.69) * mm});
            skLineSegment(sketch, "E302", {"start": v(94.08, 141.69) * mm, "end": v(96.82, 145) * mm});
            skLineSegment(sketch, "E303", {"start": v(91.22, 145.7) * mm, "end": v(93, 145.42) * mm});
            skLineSegment(sketch, "E304", {"start": v(93, 145.42) * mm, "end": v(91.25, 142.02) * mm});
            skLineSegment(sketch, "E305", {"start": v(91.25, 142.02) * mm, "end": v(92.17, 139.75) * mm});
            skLineSegment(sketch, "E306", {"start": v(92.17, 139.75) * mm, "end": v(91.9, 137.6) * mm});
            skLineSegment(sketch, "E307", {"start": v(91.9, 137.6) * mm, "end": v(89.78, 137.65) * mm});
            skLineSegment(sketch, "E308", {"start": v(89.78, 137.65) * mm, "end": v(90.2, 139.28) * mm});
            skLineSegment(sketch, "E309", {"start": v(90.2, 139.28) * mm, "end": v(89.05, 141.8) * mm});
            skLineSegment(sketch, "E310", {"start": v(89.05, 141.8) * mm, "end": v(91.22, 145.7) * mm});
            skLineSegment(sketch, "E311", {"start": v(87.02, 145.3) * mm, "end": v(85.62, 142.1) * mm});
            skLineSegment(sketch, "E312", {"start": v(85.62, 142.1) * mm, "end": v(86.94, 139.99) * mm});
            skLineSegment(sketch, "E313", {"start": v(86.94, 139.99) * mm, "end": v(87.08, 137.54) * mm});
            skLineSegment(sketch, "E314", {"start": v(87.08, 137.54) * mm, "end": v(85.28, 137.4) * mm});
            skLineSegment(sketch, "E315", {"start": v(85.28, 137.4) * mm, "end": v(85.28, 138.9) * mm});
            skLineSegment(sketch, "E316", {"start": v(85.28, 138.9) * mm, "end": v(83.87, 141.67) * mm});
            skLineSegment(sketch, "E317", {"start": v(83.87, 141.67) * mm, "end": v(85.36, 144.74) * mm});
            skLineSegment(sketch, "E318", {"start": v(55.93, 74.09) * mm, "end": v(56.91, 74.9) * mm});
            skLineSegment(sketch, "E319", {"start": v(56.91, 74.9) * mm, "end": v(58.11, 73.48) * mm});
            skLineSegment(sketch, "E320", {"start": v(58.11, 73.48) * mm, "end": v(57.16, 71.62) * mm});
            skLineSegment(sketch, "E321", {"start": v(57.77, 70.5) * mm, "end": v(58.87, 72.49) * mm});
            skLineSegment(sketch, "E322", {"start": v(58.87, 72.49) * mm, "end": v(59.78, 71.53) * mm});
            skLineSegment(sketch, "E323", {"start": v(59.78, 71.53) * mm, "end": v(58.98, 68.45) * mm});
            skLineSegment(sketch, "E324", {"start": v(60.29, 66.46) * mm, "end": v(60.29, 68.82) * mm});
            skLineSegment(sketch, "E325", {"start": v(60.29, 68.82) * mm, "end": v(61.14, 70.29) * mm});
            skLineSegment(sketch, "E326", {"start": v(61.14, 70.29) * mm, "end": v(62.46, 69.04) * mm});
            skLineSegment(sketch, "E327", {"start": v(62.46, 69.04) * mm, "end": v(61.76, 67.42) * mm});
            skLineSegment(sketch, "E328", {"start": v(61.76, 67.42) * mm, "end": v(61.76, 64.42) * mm});
            skLineSegment(sketch, "E329", {"start": v(63.92, 67.93) * mm, "end": v(65.27, 66.92) * mm});
            skLineSegment(sketch, "E330", {"start": v(65.27, 66.92) * mm, "end": v(64.53, 64.77) * mm});
            skLineSegment(sketch, "E331", {"start": v(64.53, 64.77) * mm, "end": v(65, 62.12) * mm});
            skLineSegment(sketch, "E332", {"start": v(63.92, 67.93) * mm, "end": v(62.96, 65.25) * mm});
            skLineSegment(sketch, "E333", {"start": v(65, 62.12) * mm, "end": v(63.76, 61.96) * mm});
            skLineSegment(sketch, "E334", {"start": v(62.96, 65.25) * mm, "end": v(63.1, 62.74) * mm});
            skLineSegment(sketch, "E335", {"start": v(65.96, 59.58) * mm, "end": v(67.1, 60.9) * mm});
            skLineSegment(sketch, "E336", {"start": v(67.1, 60.9) * mm, "end": v(66.53, 63.06) * mm});
            skLineSegment(sketch, "E337", {"start": v(66.53, 63.06) * mm, "end": v(67.18, 65.72) * mm});
            skLineSegment(sketch, "E338", {"start": v(67.18, 65.72) * mm, "end": v(68.5, 64.87) * mm});
            skLineSegment(sketch, "E339", {"start": v(68.5, 64.87) * mm, "end": v(67.97, 63.18) * mm});
            skLineSegment(sketch, "E340", {"start": v(67.97, 63.18) * mm, "end": v(68.75, 60.1) * mm});
            skLineSegment(sketch, "E341", {"start": v(68.75, 60.1) * mm, "end": v(67.15, 58.4) * mm});
            skLineSegment(sketch, "E342", {"start": v(70.59, 63.82) * mm, "end": v(72.1, 63.15) * mm});
            skLineSegment(sketch, "E343", {"start": v(72.1, 63.15) * mm, "end": v(71.91, 60.74) * mm});
            skLineSegment(sketch, "E344", {"start": v(71.91, 60.74) * mm, "end": v(72.84, 58.35) * mm});
            skLineSegment(sketch, "E345", {"start": v(72.84, 58.35) * mm, "end": v(70.65, 55.34) * mm});
            skLineSegment(sketch, "E346", {"start": v(70.59, 63.82) * mm, "end": v(70.27, 61.43) * mm});
            skLineSegment(sketch, "E347", {"start": v(70.27, 61.43) * mm, "end": v(71.23, 58.95) * mm});
            skLineSegment(sketch, "E348", {"start": v(71.23, 58.95) * mm, "end": v(69.59, 56.21) * mm});
            skLineSegment(sketch, "E349", {"start": v(74.87, 62.1) * mm, "end": v(76.73, 61.39) * mm});
            skLineSegment(sketch, "E350", {"start": v(76.73, 61.39) * mm, "end": v(76.58, 58.57) * mm});
            skLineSegment(sketch, "E351", {"start": v(76.58, 58.57) * mm, "end": v(77.69, 56.43) * mm});
            skLineSegment(sketch, "E352", {"start": v(77.69, 56.43) * mm, "end": v(76.7, 55.14) * mm});
            skLineSegment(sketch, "E353", {"start": v(76.7, 55.14) * mm, "end": v(76.47, 52.94) * mm});
            skLineSegment(sketch, "E354", {"start": v(76.47, 52.94) * mm, "end": v(75.04, 53.55) * mm});
            skLineSegment(sketch, "E355", {"start": v(75.04, 53.55) * mm, "end": v(75.26, 56.16) * mm});
            skLineSegment(sketch, "E356", {"start": v(75.26, 56.16) * mm, "end": v(75.74, 56.95) * mm});
            skLineSegment(sketch, "E357", {"start": v(75.74, 56.95) * mm, "end": v(74.65, 58.91) * mm});
            skLineSegment(sketch, "E358", {"start": v(74.65, 58.91) * mm, "end": v(74.87, 62.1) * mm});
            skLineSegment(sketch, "E359", {"start": v(79.18, 60.79) * mm, "end": v(80.88, 60.49) * mm});
            skLineSegment(sketch, "E360", {"start": v(80.88, 60.49) * mm, "end": v(81.16, 57.9) * mm});
            skLineSegment(sketch, "E361", {"start": v(81.16, 57.9) * mm, "end": v(82.83, 55.61) * mm});
            skLineSegment(sketch, "E362", {"start": v(82.83, 55.61) * mm, "end": v(82.1, 54.89) * mm});
            skLineSegment(sketch, "E363", {"start": v(82.1, 54.89) * mm, "end": v(82.06, 52.09) * mm});
            skLineSegment(sketch, "E364", {"start": v(82.06, 52.09) * mm, "end": v(80.2, 52.18) * mm});
            skLineSegment(sketch, "E365", {"start": v(80.2, 52.18) * mm, "end": v(80.5, 55.45) * mm});
            skLineSegment(sketch, "E366", {"start": v(80.5, 55.45) * mm, "end": v(80.82, 55.9) * mm});
            skLineSegment(sketch, "E367", {"start": v(80.82, 55.9) * mm, "end": v(79.51, 57.53) * mm});
            skLineSegment(sketch, "E368", {"start": v(79.51, 57.53) * mm, "end": v(79.18, 60.79) * mm});
            skLineSegment(sketch, "E369", {"start": v(84.23, 59.97) * mm, "end": v(86, 59.97) * mm});
            skLineSegment(sketch, "E370", {"start": v(86, 59.97) * mm, "end": v(86.39, 57.94) * mm});
            skLineSegment(sketch, "E371", {"start": v(86.39, 57.94) * mm, "end": v(88.48, 55.33) * mm});
            skLineSegment(sketch, "E372", {"start": v(88.48, 55.33) * mm, "end": v(87.88, 54.38) * mm});
            skLineSegment(sketch, "E373", {"start": v(87.88, 54.38) * mm, "end": v(88.17, 51.44) * mm});
            skLineSegment(sketch, "E374", {"start": v(88.17, 51.44) * mm, "end": v(86.48, 51.42) * mm});
            skLineSegment(sketch, "E375", {"start": v(86.48, 51.42) * mm, "end": v(86.23, 54.52) * mm});
            skLineSegment(sketch, "E376", {"start": v(86.23, 54.52) * mm, "end": v(86.69, 55.25) * mm});
            skLineSegment(sketch, "E377", {"start": v(86.69, 55.25) * mm, "end": v(85.18, 56.5) * mm});
            skLineSegment(sketch, "E378", {"start": v(85.18, 56.5) * mm, "end": v(84.23, 59.97) * mm});
            skLineSegment(sketch, "E379", {"start": v(148.38, 70.65) * mm, "end": v(147.46, 71.66) * mm});
            skLineSegment(sketch, "E380", {"start": v(147.46, 71.66) * mm, "end": v(147.27, 73.17) * mm});
            skLineSegment(sketch, "E381", {"start": v(147.27, 73.17) * mm, "end": v(145.54, 72.95) * mm});
            skLineSegment(sketch, "E382", {"start": v(145.54, 72.95) * mm, "end": v(147.3, 68.82) * mm});
            skLineSegment(sketch, "E383", {"start": v(142.2, 72.8) * mm, "end": v(143.81, 72.8) * mm});
            skLineSegment(sketch, "E384", {"start": v(143.81, 72.8) * mm, "end": v(144.63, 70.28) * mm});
            skLineSegment(sketch, "E385", {"start": v(144.63, 70.28) * mm, "end": v(145.32, 69.33) * mm});
            skLineSegment(sketch, "E386", {"start": v(145.32, 69.33) * mm, "end": v(143.81, 65.56) * mm});
            skLineSegment(sketch, "E387", {"start": v(143.81, 65.56) * mm, "end": v(142.15, 65.5) * mm});
            skLineSegment(sketch, "E388", {"start": v(142.15, 65.5) * mm, "end": v(143.9, 69.11) * mm});
            skLineSegment(sketch, "E389", {"start": v(143.9, 69.11) * mm, "end": v(142.2, 72.8) * mm});
            skLineSegment(sketch, "E390", {"start": v(137.68, 70.53) * mm, "end": v(139.19, 71.91) * mm});
            skLineSegment(sketch, "E391", {"start": v(139.19, 71.91) * mm, "end": v(141.36, 68.67) * mm});
            skLineSegment(sketch, "E392", {"start": v(141.36, 68.67) * mm, "end": v(139.82, 64.7) * mm});
            skLineSegment(sketch, "E393", {"start": v(139.82, 64.7) * mm, "end": v(138.09, 64.62) * mm});
            skLineSegment(sketch, "E394", {"start": v(138.09, 64.62) * mm, "end": v(139.38, 68.26) * mm});
            skLineSegment(sketch, "E395", {"start": v(139.38, 68.26) * mm, "end": v(137.68, 70.53) * mm});
            skLineSegment(sketch, "E396", {"start": v(134.52, 67.4) * mm, "end": v(135.64, 68.2) * mm});
            skLineSegment(sketch, "E397", {"start": v(135.64, 68.2) * mm, "end": v(136.8, 67.57) * mm});
            skLineSegment(sketch, "E398", {"start": v(136.8, 67.57) * mm, "end": v(135.61, 63.93) * mm});
            skLineSegment(sketch, "E399", {"start": v(135.61, 63.93) * mm, "end": v(133.77, 63.27) * mm});
            skLineSegment(sketch, "E400", {"start": v(133.77, 63.27) * mm, "end": v(134.84, 66.94) * mm});
            skLineSegment(sketch, "E401", {"start": v(134.84, 66.94) * mm, "end": v(134.52, 67.4) * mm});
            skArc(sketch, "E402", {"start": v(81.9, 111.8) * mm, "mid": v(80.25, 110.12) * mm, "end": v(79.75, 107.82) * mm});
            skArc(sketch, "E403", {"start": v(81.9, 111.8) * mm, "mid": v(81.47, 109.82) * mm, "end": v(81.85, 107.85) * mm});
            skLineSegment(sketch, "E404", {"start": v(79.75, 107.82) * mm, "end": v(81.85, 107.85) * mm});
            skSolve(sketch);
        }
        {
            var Q0;
            Q0=makeQuery(id+"F0.imprint","IMPRINT",FACE,{"disambiguationData":[TD([[makeQuery(id+"F0.imprint","IMPRINT",EDGE,{"derivedFrom":sQuery(id+"F0.wireOp",EDGE,"E2")}),1.0]])]});
            var Q1;
            Q1=makeQuery(id+"F0.imprint","IMPRINT",FACE,{"disambiguationData":[TD([[makeQuery(id+"F0.imprint","IMPRINT",EDGE,{"derivedFrom":sQuery(id+"F0.wireOp",EDGE,"E9")}),1.0]])]});
            var Q2;
            Q2=makeQuery(id+"F0.imprint","IMPRINT",FACE,{"disambiguationData":[TD([[makeQuery(id+"F0.imprint","IMPRINT",EDGE,{"derivedFrom":sQuery(id+"F0.wireOp",EDGE,"E4")}),1.0]])]});
            var Q3;
            Q3=makeQuery(id+"F0.imprint","IMPRINT",FACE,{"disambiguationData":[TD([[makeQuery(id+"F0.imprint","IMPRINT",EDGE,{"derivedFrom":sQuery(id+"F0.wireOp",EDGE,"E6")}),1.0]])]});
            var Q4;
            Q4=makeQuery(id+"F0.imprint","IMPRINT",FACE,{"disambiguationData":[TD([[makeQuery(id+"F0.imprint","IMPRINT",EDGE,{"derivedFrom":sQuery(id+"F0.wireOp",EDGE,"E43")}),-1.0]])]});
            var Q5;
            Q5=makeQuery(id+"F0.imprint","IMPRINT",FACE,{"disambiguationData":[TD([[makeQuery(id+"F0.imprint","IMPRINT",EDGE,{"derivedFrom":sQuery(id+"F0.wireOp",EDGE,"E46")}),-1.0]])]});
            var Q6;
            Q6=makeQuery(id+"F0.imprint","IMPRINT",FACE,{"disambiguationData":[TD([[makeQuery(id+"F0.imprint","IMPRINT",EDGE,{"derivedFrom":sQuery(id+"F0.wireOp",EDGE,"E17")}),1.0]])]});
            var Q7;
            Q7=makeQuery(id+"F0.imprint","IMPRINT",FACE,{"disambiguationData":[TD([[makeQuery(id+"F0.imprint","IMPRINT",EDGE,{"derivedFrom":sQuery(id+"F0.wireOp",EDGE,"E47")}),1.0]])]});
            var Q8;
            Q8=makeQuery(id+"F0.imprint","IMPRINT",FACE,{"disambiguationData":[TD([[makeQuery(id+"F0.imprint","IMPRINT",EDGE,{"derivedFrom":sQuery(id+"F0.wireOp",EDGE,"E101")}),1.0]])]});
            var Q9;
            Q9=makeQuery(id+"F0.imprint","IMPRINT",FACE,{"disambiguationData":[TD([[makeQuery(id+"F0.imprint","IMPRINT",EDGE,{"derivedFrom":sQuery(id+"F0.wireOp",EDGE,"E109")}),1.0]])]});
            var Q10;
            Q10=makeQuery(id+"F0.imprint","IMPRINT",FACE,{"disambiguationData":[TD([[makeQuery(id+"F0.imprint","IMPRINT",EDGE,{"derivedFrom":sQuery(id+"F0.wireOp",EDGE,"E97")}),-1.0]])]});
            var Q11;
            Q11=makeQuery(id+"F0.imprint","IMPRINT",FACE,{"disambiguationData":[TD([[makeQuery(id+"F0.imprint","IMPRINT",EDGE,{"derivedFrom":sQuery(id+"F0.wireOp",EDGE,"E89")}),-1.0]])]});
            var Q12;
            Q12=makeQuery(id+"F0.imprint","IMPRINT",FACE,{"disambiguationData":[TD([[makeQuery(id+"F0.imprint","IMPRINT",EDGE,{"derivedFrom":sQuery(id+"F0.wireOp",EDGE,"E81")}),-1.0]])]});
            var Q13;
            Q13=makeQuery(id+"F0.imprint","IMPRINT",FACE,{"disambiguationData":[TD([[makeQuery(id+"F0.imprint","IMPRINT",EDGE,{"derivedFrom":sQuery(id+"F0.wireOp",EDGE,"E79")}),-1.0]])]});
            var Q14;
            Q14=makeQuery(id+"F0.imprint","IMPRINT",FACE,{"disambiguationData":[TD([[makeQuery(id+"F0.imprint","IMPRINT",EDGE,{"derivedFrom":sQuery(id+"F0.wireOp",EDGE,"E162")}),-1.0]])]});
            var Q15;
            Q15=makeQuery(id+"F0.imprint","IMPRINT",FACE,{"disambiguationData":[TD([[makeQuery(id+"F0.imprint","IMPRINT",EDGE,{"derivedFrom":sQuery(id+"F0.wireOp",EDGE,"E193")}),-1.0]])]});
            var Q16;
            Q16=makeQuery(id+"F0.imprint","IMPRINT",FACE,{"disambiguationData":[TD([[makeQuery(id+"F0.imprint","IMPRINT",EDGE,{"derivedFrom":sQuery(id+"F0.wireOp",EDGE,"E196")}),-1.0]])]});
            var Q17;
            Q17=makeQuery(id+"F0.imprint","IMPRINT",FACE,{"disambiguationData":[TD([[makeQuery(id+"F0.imprint","IMPRINT",EDGE,{"derivedFrom":sQuery(id+"F0.wireOp",EDGE,"E118")}),1.0]])]});
            var Q18;
            Q18=makeQuery(id+"F0.imprint","IMPRINT",FACE,{"disambiguationData":[TD([[makeQuery(id+"F0.imprint","IMPRINT",EDGE,{"derivedFrom":sQuery(id+"F0.wireOp",EDGE,"E123")}),1.0]])]});
            var Q19;
            Q19=makeQuery(id+"F0.imprint","IMPRINT",FACE,{"disambiguationData":[TD([[makeQuery(id+"F0.imprint","IMPRINT",EDGE,{"derivedFrom":sQuery(id+"F0.wireOp",EDGE,"E170")}),-1.0]])]});
            var Q20;
            Q20=makeQuery(id+"F0.imprint","IMPRINT",FACE,{"disambiguationData":[TD([[makeQuery(id+"F0.imprint","IMPRINT",EDGE,{"derivedFrom":sQuery(id+"F0.wireOp",EDGE,"E172")}),1.0]])]});
            var Q21;
            Q21=makeQuery(id+"F0.imprint","IMPRINT",FACE,{"disambiguationData":[TD([[makeQuery(id+"F0.imprint","IMPRINT",EDGE,{"derivedFrom":sQuery(id+"F0.wireOp",EDGE,"E142")}),1.0]])]});
            var Q22;
            Q22=makeQuery(id+"F0.imprint","IMPRINT",FACE,{"disambiguationData":[TD([[makeQuery(id+"F0.imprint","IMPRINT",EDGE,{"derivedFrom":sQuery(id+"F0.wireOp",EDGE,"E132")}),1.0]])]});
            var Q23;
            Q23=makeQuery(id+"F0.imprint","IMPRINT",FACE,{"disambiguationData":[TD([[makeQuery(id+"F0.imprint","IMPRINT",EDGE,{"derivedFrom":sQuery(id+"F0.wireOp",EDGE,"E152")}),-1.0]])]});
            var Q24;
            Q24=makeQuery(id+"F0.imprint","IMPRINT",FACE,{"disambiguationData":[TD([[makeQuery(id+"F0.imprint","IMPRINT",EDGE,{"derivedFrom":sQuery(id+"F0.wireOp",EDGE,"E257")}),-1.0]])]});
            var Q25;
            Q25=makeQuery(id+"F0.imprint","IMPRINT",FACE,{"disambiguationData":[TD([[makeQuery(id+"F0.imprint","IMPRINT",EDGE,{"derivedFrom":sQuery(id+"F0.wireOp",EDGE,"E261")}),1.0]])]});
            var Q26;
            Q26=makeQuery(id+"F0.imprint","IMPRINT",FACE,{"disambiguationData":[TD([[makeQuery(id+"F0.imprint","IMPRINT",EDGE,{"derivedFrom":sQuery(id+"F0.wireOp",EDGE,"E233")}),-1.0]])]});
            var Q27;
            Q27=makeQuery(id+"F0.imprint","IMPRINT",FACE,{"disambiguationData":[TD([[makeQuery(id+"F0.imprint","IMPRINT",EDGE,{"derivedFrom":sQuery(id+"F0.wireOp",EDGE,"E247")}),-1.0]])]});
            var Q28;
            Q28=makeQuery(id+"F0.imprint","IMPRINT",FACE,{"disambiguationData":[TD([[makeQuery(id+"F0.imprint","IMPRINT",EDGE,{"derivedFrom":sQuery(id+"F0.wireOp",EDGE,"E241")}),1.0]])]});
            var Q29;
            Q29=makeQuery(id+"F0.imprint","IMPRINT",FACE,{"disambiguationData":[TD([[makeQuery(id+"F0.imprint","IMPRINT",EDGE,{"derivedFrom":sQuery(id+"F0.wireOp",EDGE,"E217")}),-1.0]])]});
            var Q30;
            Q30=makeQuery(id+"F0.imprint","IMPRINT",FACE,{"disambiguationData":[TD([[makeQuery(id+"F0.imprint","IMPRINT",EDGE,{"derivedFrom":sQuery(id+"F0.wireOp",EDGE,"E209")}),-1.0]])]});
            var Q31;
            Q31=makeQuery(id+"F0.imprint","IMPRINT",FACE,{"disambiguationData":[TD([[makeQuery(id+"F0.imprint","IMPRINT",EDGE,{"derivedFrom":sQuery(id+"F0.wireOp",EDGE,"E225")}),-1.0]])]});
            var Q32;
            Q32=makeQuery(id+"F0.imprint","IMPRINT",FACE,{"disambiguationData":[TD([[makeQuery(id+"F0.imprint","IMPRINT",EDGE,{"derivedFrom":sQuery(id+"F0.wireOp",EDGE,"E271")}),1.0]])]});
            var Q33;
            Q33=makeQuery(id+"F0.imprint","IMPRINT",FACE,{"disambiguationData":[TD([[makeQuery(id+"F0.imprint","IMPRINT",EDGE,{"derivedFrom":sQuery(id+"F0.wireOp",EDGE,"E275")}),1.0]])]});
            var Q34;
            {var subQ1=sQuery(id+"F0.wireOp",EDGE,"E311");Q34=makeQuery(id+"F0.imprint","IMPRINT",FACE,{"disambiguationData":[TD([[makeQuery(id+"F0.imprint","IMPRINT",EDGE,{"derivedFrom":subQ1}),-1.0]])]});}
            var Q35;
            Q35=makeQuery(id+"F0.imprint","IMPRINT",FACE,{"disambiguationData":[TD([[makeQuery(id+"F0.imprint","IMPRINT",EDGE,{"derivedFrom":sQuery(id+"F0.wireOp",EDGE,"E303")}),-1.0]])]});
            var Q36;
            Q36=makeQuery(id+"F0.imprint","IMPRINT",FACE,{"disambiguationData":[TD([[makeQuery(id+"F0.imprint","IMPRINT",EDGE,{"derivedFrom":sQuery(id+"F0.wireOp",EDGE,"E295")}),-1.0]])]});
            var Q37;
            Q37=makeQuery(id+"F0.imprint","IMPRINT",FACE,{"disambiguationData":[TD([[makeQuery(id+"F0.imprint","IMPRINT",EDGE,{"derivedFrom":sQuery(id+"F0.wireOp",EDGE,"E289")}),-1.0]])]});
            var Q38;
            Q38=makeQuery(id+"F0.imprint","IMPRINT",FACE,{"disambiguationData":[TD([[makeQuery(id+"F0.imprint","IMPRINT",EDGE,{"derivedFrom":sQuery(id+"F0.wireOp",EDGE,"E283")}),-1.0]])]});
            var Q39;
            Q39=makeQuery(id+"F0.imprint","IMPRINT",FACE,{"disambiguationData":[TD([[makeQuery(id+"F0.imprint","IMPRINT",EDGE,{"derivedFrom":sQuery(id+"F0.wireOp",EDGE,"E279")}),-1.0]])]});
            var Q40;
            {var subQ1=sQuery(id+"F0.wireOp",EDGE,"E318");Q40=makeQuery(id+"F0.imprint","IMPRINT",FACE,{"disambiguationData":[TD([[makeQuery(id+"F0.imprint","IMPRINT",EDGE,{"derivedFrom":subQ1}),-1.0]])]});}
            var Q41;
            {var subQ1=sQuery(id+"F0.wireOp",EDGE,"E321");Q41=makeQuery(id+"F0.imprint","IMPRINT",FACE,{"disambiguationData":[TD([[makeQuery(id+"F0.imprint","IMPRINT",EDGE,{"derivedFrom":subQ1}),-1.0]])]});}
            var Q42;
            {var subQ1=sQuery(id+"F0.wireOp",EDGE,"E324");Q42=makeQuery(id+"F0.imprint","IMPRINT",FACE,{"disambiguationData":[TD([[makeQuery(id+"F0.imprint","IMPRINT",EDGE,{"derivedFrom":subQ1}),-1.0]])]});}
            var Q43;
            Q43=makeQuery(id+"F0.imprint","IMPRINT",FACE,{"disambiguationData":[TD([[makeQuery(id+"F0.imprint","IMPRINT",EDGE,{"derivedFrom":sQuery(id+"F0.wireOp",EDGE,"E329")}),-1.0]])]});
            var Q44;
            {var subQ1=sQuery(id+"F0.wireOp",EDGE,"E335");Q44=makeQuery(id+"F0.imprint","IMPRINT",FACE,{"disambiguationData":[TD([[makeQuery(id+"F0.imprint","IMPRINT",EDGE,{"derivedFrom":subQ1}),-1.0]])]});}
            var Q45;
            Q45=makeQuery(id+"F0.imprint","IMPRINT",FACE,{"disambiguationData":[TD([[makeQuery(id+"F0.imprint","IMPRINT",EDGE,{"derivedFrom":sQuery(id+"F0.wireOp",EDGE,"E342")}),-1.0]])]});
            var Q46;
            Q46=makeQuery(id+"F0.imprint","IMPRINT",FACE,{"disambiguationData":[TD([[makeQuery(id+"F0.imprint","IMPRINT",EDGE,{"derivedFrom":sQuery(id+"F0.wireOp",EDGE,"E349")}),-1.0]])]});
            var Q47;
            Q47=makeQuery(id+"F0.imprint","IMPRINT",FACE,{"disambiguationData":[TD([[makeQuery(id+"F0.imprint","IMPRINT",EDGE,{"derivedFrom":sQuery(id+"F0.wireOp",EDGE,"E359")}),-1.0]])]});
            var Q48;
            Q48=makeQuery(id+"F0.imprint","IMPRINT",FACE,{"disambiguationData":[TD([[makeQuery(id+"F0.imprint","IMPRINT",EDGE,{"derivedFrom":sQuery(id+"F0.wireOp",EDGE,"E369")}),-1.0]])]});
            var Q49;
            Q49=makeQuery(id+"F0.imprint","IMPRINT",FACE,{"disambiguationData":[TD([[makeQuery(id+"F0.imprint","IMPRINT",EDGE,{"derivedFrom":sQuery(id+"F0.wireOp",EDGE,"E383")}),-1.0]])]});
            var Q50;
            {var subQ1=sQuery(id+"F0.wireOp",EDGE,"E379");Q50=makeQuery(id+"F0.imprint","IMPRINT",FACE,{"disambiguationData":[TD([[makeQuery(id+"F0.imprint","IMPRINT",EDGE,{"derivedFrom":subQ1}),1.0]])]});}
            var Q51;
            Q51=makeQuery(id+"F0.imprint","IMPRINT",FACE,{"disambiguationData":[TD([[makeQuery(id+"F0.imprint","IMPRINT",EDGE,{"derivedFrom":sQuery(id+"F0.wireOp",EDGE,"E390")}),-1.0]])]});
            var Q52;
            Q52=makeQuery(id+"F0.imprint","IMPRINT",FACE,{"disambiguationData":[TD([[makeQuery(id+"F0.imprint","IMPRINT",EDGE,{"derivedFrom":sQuery(id+"F0.wireOp",EDGE,"E396")}),-1.0]])]});
            var Q53;
            Q53=makeQuery(id+"F0.imprint","IMPRINT",FACE,{"disambiguationData":[TD([[makeQuery(id+"F0.imprint","IMPRINT",EDGE,{"derivedFrom":sQuery(id+"F0.wireOp",EDGE,"E99")}),1.0]])]});
            extrude(context, id + "F1", {"entities" : qUnion([Q0, Q1, Q2, Q3, Q4, Q5, Q6, Q7, Q8, Q9, Q10, Q11, Q12, Q13, Q14, Q15, Q16, Q17, Q18, Q19, Q20, Q21, Q22, Q23, Q24, Q25, Q26, Q27, Q28, Q29, Q30, Q31, Q32, Q33, Q34, Q35, Q36, Q37, Q38, Q39, Q40, Q41, Q42, Q43, Q44, Q45, Q46, Q47, Q48, Q49, Q50, Q51, Q52, Q53]), "depth" : 6.35 * mm});
        }
    });
